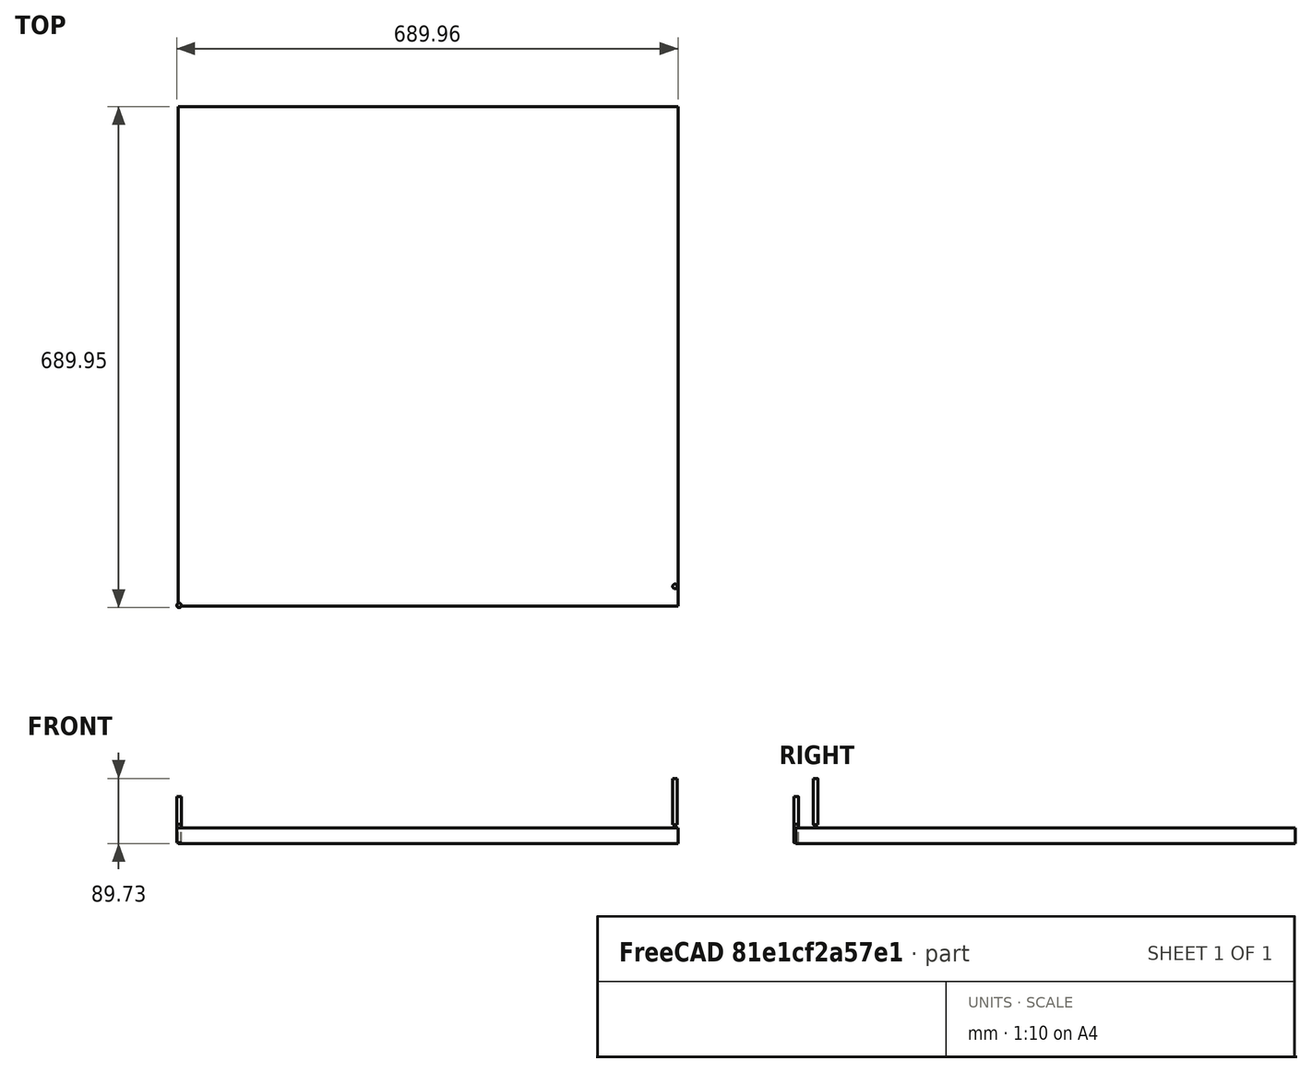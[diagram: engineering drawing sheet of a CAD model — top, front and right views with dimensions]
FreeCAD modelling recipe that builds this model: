
FCSTD DOCUMENT  (FreeCAD 0.21R33771 (Git))
Label: front_panel_try2
License: All rights reserved
LicenseURL: http://en.wikipedia.org/wiki/All_rights_reserved
objects: Part::FeaturePython×6, Part::Box×5, Path::FeaturePython×4, Mesh::FeaturePython×4, App::DocumentObjectGroup×3, Part::Cylinder×2, Part::MultiFuse×1, Part::Cut×1, App::FeaturePython×1
note: 16 computed .brp shape members not serialized (recipe doc carries the construction recipe); baked Part::Feature solids carry a one-line shape summary decoded from their .brp

FEATURE [Part::Box] cube
  AttacherType = Attacher::AttachEngine3D
  Height = 9.6266
  Length = 635
  Width = 635
FEATURE [Part::Cylinder] cylinder
  Angle = 360
  AttacherType = Attacher::AttachEngine3D
  FirstAngle = 0
  Height = 9.6266
  Radius = 25.4
  SecondAngle = 0
FEATURE [Part::FeaturePython] minkowski  # WARN: FeaturePython — macro-defined, semantics opaque (R4)
  Arguments = {'convexity': '0'}
  Children = -> [cube,cylinder]
  Operation = minkowski
  Placement = pos=(25.4,25.4,0) rot=(0,0,1;0rad)
FEATURE [Part::Cylinder] cylinder001
  Angle = 360
  AttacherType = Attacher::AttachEngine3D
  FirstAngle = 0
  Height = 254
  Placement = pos=(342.9,342.9,-127) rot=(0,0,1;0rad)
  Radius = 275.272
  SecondAngle = 0
FEATURE [Part::Box] cube001
  AttacherType = Attacher::AttachEngine3D
  Height = 10.525
  Length = 736.6
  Placement = pos=(-25.4,20.6375,9.7282) rot=(0,0,1;0rad)
  Width = 8.73125
FEATURE [Part::Box] cube002
  AttacherType = Attacher::AttachEngine3D
  Height = 10.525
  Length = 736.6
  Placement = pos=(-25.4,656.431,9.7282) rot=(0,0,1;0rad)
  Width = 8.73125
FEATURE [Part::Box] cube003
  AttacherType = Attacher::AttachEngine3D
  Height = 10.525
  Length = 8.73125
  Placement = pos=(20.6375,29.3687,9.7282) rot=(0,0,1;0rad)
  Width = 627.539
FEATURE [Part::Box] cube004
  AttacherType = Attacher::AttachEngine3D
  Height = 10.525
  Length = 8.73125
  Placement = pos=(656.431,29.3687,9.7282) rot=(0,0,1;0rad)
  Width = 627.539
FEATURE [Part::MultiFuse] union
  Shapes = -> [cylinder001,cube001,cube002,cube003,cube004]
FEATURE [Part::Cut] difference
  Base = -> minkowski
  Tool = -> union
FEATURE [App::FeaturePython] SetupSheet  # Path/CAM operation (typed FeaturePython)
  ClearanceHeightExpression = OpStockZMax+SetupSheet.ClearanceHeightOffset
  ClearanceHeightOffset = 5
  CoolantMode = 0
  CoolantModes = None | Flood | Mist
  FinalDepthExpression = OpFinalDepth
  HorizRapid = 0
  SafeHeightExpression = OpStockZMax+SetupSheet.SafeHeightOffset
  SafeHeightOffset = 3
  StartDepthExpression = OpStartDepth
  StepDownExpression = OpToolDiameter
  VertRapid = 0
FEATURE [Part::FeaturePython] Clone  label="Model-difference"  # Draft clone (typed FeaturePython)
  AttacherType = Attacher::AttachEngine3D
  Fuse = false
  Objects = -> [difference]
  PathResource = Model
  Scale = (1,1,1)
FEATURE [App::DocumentObjectGroup] Model
  Group = -> [Clone]
FEATURE [Part::FeaturePython] Stock  # WARN: FeaturePython — macro-defined, semantics opaque (R4)
  Base = -> Model
  ExtXneg = 0.9906
  ExtXpos = 0.9906
  ExtYneg = 0.9906
  ExtYpos = 0.9906
  ExtZneg = 0.9906
  ExtZpos = 0.9906
  Placement = pos=(3.8147e-07,0.00790062,0) rot=(0,0,1;0rad)
  StockType = FromBase
FEATURE [Part::FeaturePython] ToolBit001  label="SpeTool 1/4" Downcut Carbide End Mill"  # Path/CAM toolbit (typed FeaturePython)
  BitPropertyNames = Chipload | CuttingEdgeHeight | Diameter | Flutes | Length | Material | ShankDiameter | SpindleDirection
  BitShape = <path>
  Chipload = 0
  CuttingEdgeHeight = 25.4
  Diameter = 6.35
  File = <userpath>/.config/FreeCAD-tools/Bit/1-4inch_endmill.fctb
  Flutes = 2
  Length = 63.5
  Material = 1
  ShankDiameter = 6.35
  ShapeName = endmill
  SpindleDirection = 0
FEATURE [Path::FeaturePython] TC__SpeTool_1_4__Downcut_Carbide_End_Mill  label="TC: SpeTool 1/4" Downcut Carbide End Mill"  # Path/CAM operation (typed FeaturePython)
  HorizFeed = 0
  HorizRapid = 0
  SpindleDir = 0
  SpindleSpeed = 0
  Tool = -> ToolBit001
  ToolNumber = 1
  VertFeed = 0
  VertRapid = 0
  expr: HorizRapid = SetupSheet.HorizRapid
  expr: VertRapid = SetupSheet.VertRapid
FEATURE [Part::FeaturePython] ToolBit002  label="SpeTool 3/16" Downcut Carbide End Mill"  # Path/CAM toolbit (typed FeaturePython)
  BitPropertyNames = Chipload | CuttingEdgeHeight | Diameter | Flutes | Length | Material | ShankDiameter | SpindleDirection
  BitShape = <path>
  Chipload = 0
  CuttingEdgeHeight = 25.4
  Diameter = 4.7498
  File = <userpath>/.config/FreeCAD-tools/Bit/3-16inch_endmill.fctb
  Flutes = 2
  Length = 63.5
  Material = 1
  ShankDiameter = 6.35
  ShapeName = endmill
  SpindleDirection = 0
FEATURE [Path::FeaturePython] TC__SpeTool_3_16__Downcut_Carbide_End_Mill  label="TC: SpeTool 3/16" Downcut Carbide End Mill"  # Path/CAM operation (typed FeaturePython)
  HorizFeed = 0
  HorizRapid = 0
  SpindleDir = 0
  SpindleSpeed = 0
  Tool = -> ToolBit002
  ToolNumber = 2
  VertFeed = 0
  VertRapid = 0
  expr: HorizRapid = SetupSheet.HorizRapid
  expr: VertRapid = SetupSheet.VertRapid
FEATURE [App::DocumentObjectGroup] Tools
  Group = -> [TC__SpeTool_1_4__Downcut_Carbide_End_Mill,TC__SpeTool_3_16__Downcut_Carbide_End_Mill]
FEATURE [Path::FeaturePython] Pocket_Shape  # Path/CAM operation (typed FeaturePython)
  Active = true
  AreaParams:
    Tolerance = 1e-07
    FitArcs = True
    Simplify = False
    CleanDistance = 0.0
    Accuracy = 0.01
    Unit = 1.0
    MinArcPoints = 4
    MaxArcPoints = 100
    ClipperScale = 10000000.0
    Fill = 0
    Coplanar = 0
    Reorient = True
    Outline = False
    Explode = False
    OpenMode = 0
    Deflection = 0.01
    SubjectFill = 0
    ClipFill = 0
    Offset = 0.0
    ExtraPass = 0
    Stepover = 0.0
    LastStepover = 0.0
    JoinType = 0
    EndType = 0
    MiterLimit = 2.0
    RoundPrecision = 0.0
    PocketMode = 2
    ToolRadius = 3.175
    PocketExtraOffset = 0.0
    PocketStepover = 6.35
    PocketLastStepover = 0.0
    FromCenter = True
    Angle = 45.0
    AngleShift = 0.0
    Shift = 0.0
    Thicken = False
    SectionCount = -1
    Stepdown = 1.0
    SectionOffset = 0.0
    SectionTolerance = 1e-07
    SectionMode = 2
    Project = False
  Base = -> [Clone]
  ClearanceHeight = 25.2438
  CoolantMode = 0
  CutMode = 0
  CycleTime = Cycletime Error
  ExtensionCorners = true
  ExtensionFeature = -> [Clone]
  ExtensionLengthDefault = 6.35
  ExtraOffset = 0
  FinalDepth = 9.7282
  FinishDepth = 0
  KeepToolDown = false
  MinTravel = false
  OffsetPattern = 1
  OpFinalDepth = 9.7282
  OpStartDepth = 20.2438
  OpStockZMax = 20.2438
  OpStockZMin = -0.9906
  OpToolDiameter = 6.35
  PathParams = {'orientation': 1, 'feedrate': 0.0, 'feedrate_v': 0.0, 'verbose': True, 'resume_height': 23.24380053100589, 'retraction': 25.24380053100589, 'return_end': True, 'preamble': False}
  PocketLastStepOver = 0
  SafeHeight = 23.2438
  SplitArcs = false
  StartAt = 0
  StartDepth = 20.2438
  StartPoint = (0,0,0)
  StepDown = 3.175
  StepOver = 100
  ToolController = -> TC__SpeTool_1_4__Downcut_Carbide_End_Mill
  UseOutline = false
  UseStartPoint = false
  ZigZagAngle = 45
  expr: ClearanceHeight = OpStockZMax + SetupSheet.ClearanceHeightOffset
  expr: FinalDepth = OpFinalDepth
  expr: SafeHeight = OpStockZMax + SetupSheet.SafeHeightOffset
  expr: StartDepth = OpStartDepth
  expr: StepDown = OpToolDiameter / 2
FEATURE [App::DocumentObjectGroup] Operations
  Group = -> [Pocket_Shape]
FEATURE [Path::FeaturePython] Job  # Path/CAM operation (typed FeaturePython)
  CycleTime = 00:00:00
  Fixtures = G54
  GeometryTolerance = 0
  JobType = 0
  Model = -> Model
  Operations = -> Operations
  OrderOutputBy = 0
  PostProcessor = 1
  SetupSheet = -> SetupSheet
  SplitOutput = false
  Stock = -> Stock
  Tools = -> Tools
FEATURE [Mesh::FeaturePython] CutMaterial  # WARN: FeaturePython — macro-defined, semantics opaque (R4)
FEATURE [Part::FeaturePython] CutTool  # WARN: FeaturePython — macro-defined, semantics opaque (R4)
  Placement = pos=(682.736,26.1937,25.2438) rot=(0,0,1;0rad)
FEATURE [Mesh::FeaturePython] CutMaterial001  # WARN: FeaturePython — macro-defined, semantics opaque (R4)
FEATURE [Mesh::FeaturePython] CutMaterialIn  # WARN: FeaturePython — macro-defined, semantics opaque (R4)
FEATURE [Mesh::FeaturePython] CutMaterial002  # WARN: FeaturePython — macro-defined, semantics opaque (R4)
note: 2 file-system paths scrubbed to <path> (originals preserved in the JSON sidecar)
